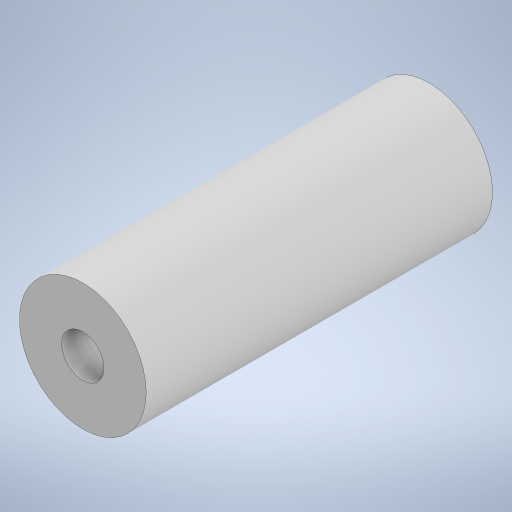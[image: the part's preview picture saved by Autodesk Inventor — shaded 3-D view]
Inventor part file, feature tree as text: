
AUTODESK INVENTOR PART (.ipt)
format: ipt  version: 2024.3 (Build 283343000, 343)  size: 206,848 bytes
history: native  units: mm
features: other x1, extrude x1, sketch x1
ambient origin geometry x8: Origin, YZ Plane, XZ Plane, XY Plane, X Axis, Y Axis, Z Axis, Center Point
bodies: Body1 (feature_tree)
feature tree (3):
  other  "ソリッド1"
  extrude  "押し出し1"  Depth=15.0mm
  sketch  "スケッチ1"
